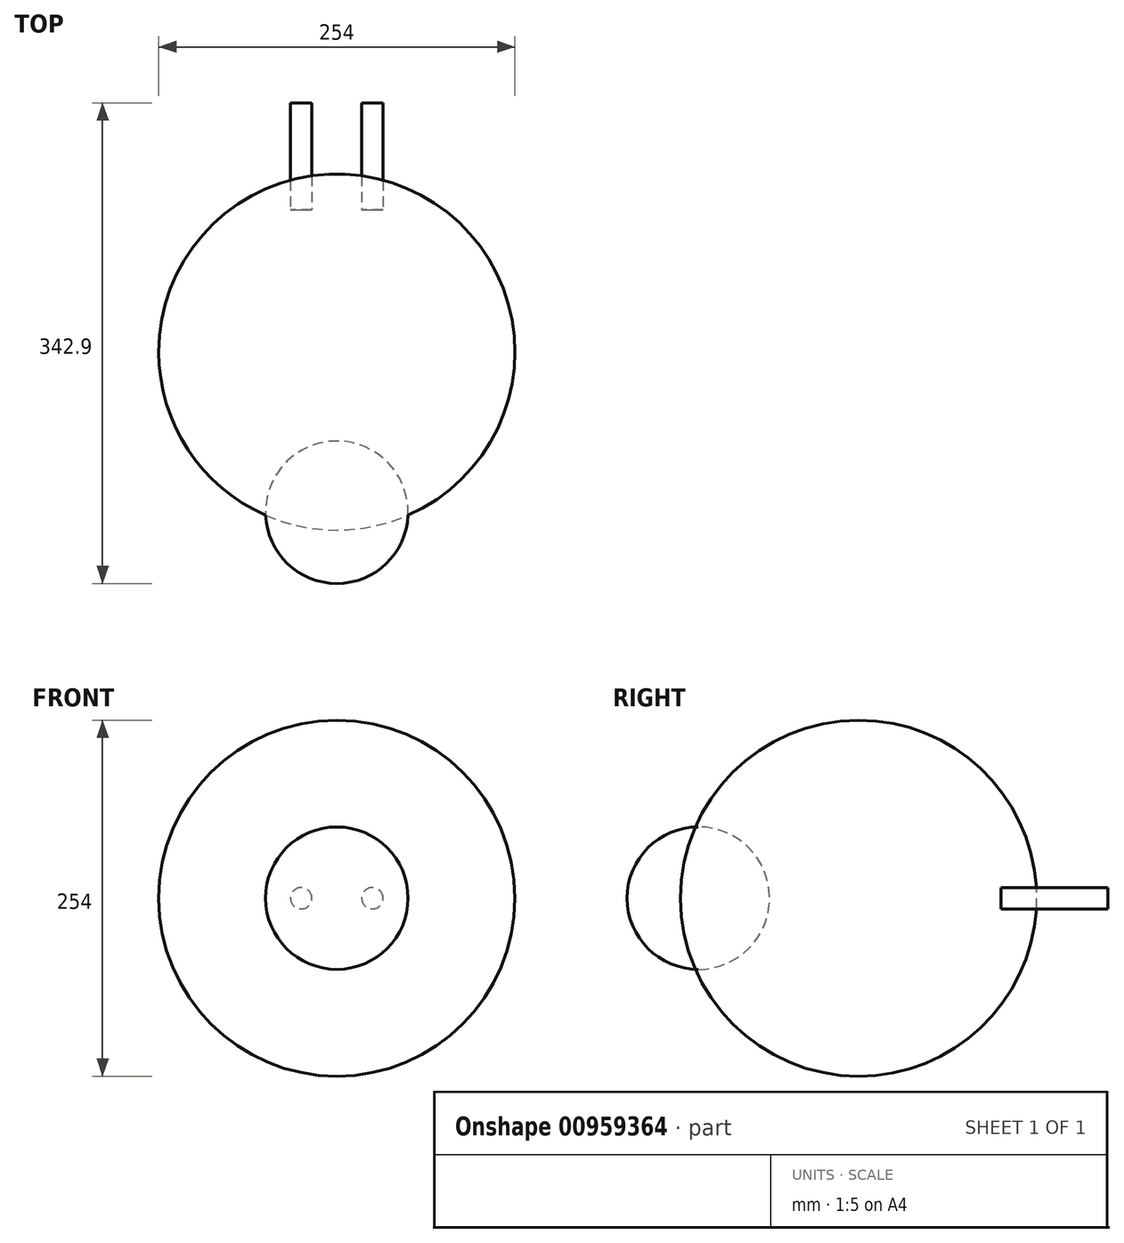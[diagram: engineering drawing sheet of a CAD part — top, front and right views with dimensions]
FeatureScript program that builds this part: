
annotation { "Feature Type Name" : "Feature", "Feature Type Description" : "" }
export const myFeature = defineFeature(function(context is Context, id is Id, definition is map)
    precondition{}
    {
        {
            var Q0;
            Q0=qCreatedBy(makeId("Front.planeOp"),FACE);
            var sketch = newSketch(context, id + "F0", { "sketchPlane" : qUnion([Q0])});
            skArc(sketch, "E0", {"start": v(0, -127) * mm, "mid": v(127, 0) * mm, "end": v(0, 127) * mm});
            skLineSegment(sketch, "E1", {"start": v(0, 127) * mm, "end": v(0, -127) * mm});
            skSolve(sketch);
        }
        {
            var Q0;
            Q0=makeQuery(id+"F0.imprint","IMPRINT",FACE,{"disambiguationData":[TD([[makeQuery(id+"F0.imprint","IMPRINT",EDGE,{"derivedFrom":sQuery(id+"F0.wireOp",EDGE,"E0")}),1.0]])]});
            var Q1;
            Q1=sQuery(id+"F0.wireOp",EDGE,"E1");
            revolve(context, id + "F1", {"surfaceOperationType" : NewSurfaceOperationType.NEW, "entities" : qUnion([Q0]), "axis" : qUnion([Q1]), "revolveType" : RevolveType.FULL});
        }
        {
            var Q0;
            Q0=makeQuery(id+"F0.imprint","IMPRINT",FACE,{"disambiguationData":[TD([[makeQuery(id+"F0.imprint","IMPRINT",EDGE,{"derivedFrom":sQuery(id+"F0.wireOp",EDGE,"E0")}),1.0]])]});
            cPlane(context, id + "F2", {"entities" : qUnion([Q0]), "cplaneType" : CPlaneType.OFFSET, "offset" : 114.3 * mm, "width" : 152.4 * mm, "height" : 152.4 * mm});
        }
        {
            var Q0;
            Q0=qCreatedBy(id+"F2.planeOp",FACE);
            var sketch = newSketch(context, id + "F3", { "sketchPlane" : qUnion([Q0])});
            skArc(sketch, "E2", {"start": v(0, -50.8) * mm, "mid": v(50.8, 0) * mm, "end": v(0, 50.8) * mm});
            skLineSegment(sketch, "E3", {"start": v(0, 50.8) * mm, "end": v(0, -50.8) * mm});
            skSolve(sketch);
        }
        {
            var Q0;
            Q0=makeQuery(id+"F3.imprint","IMPRINT",FACE,{"disambiguationData":[TD([[makeQuery(id+"F3.imprint","IMPRINT",EDGE,{"derivedFrom":sQuery(id+"F3.wireOp",EDGE,"E2")}),1.0]])]});
            var Q1;
            Q1=sQuery(id+"F3.wireOp",EDGE,"E3");
            revolve(context, id + "F4", {"surfaceOperationType" : NewSurfaceOperationType.NEW, "entities" : qUnion([Q0]), "axis" : qUnion([Q1]), "revolveType" : RevolveType.FULL});
        }
        {
            var Q0;
            Q0=qCreatedBy(makeId("Top.planeOp"),FACE);
            cPlane(context, id + "F5", {"entities" : qUnion([Q0]), "cplaneType" : CPlaneType.OFFSET, "offset" : 0 * mm, "oppositeDirection" : true, "width" : 152.4 * mm, "height" : 152.4 * mm});
        }
        {
            var Q0;
            Q0=qCreatedBy(id+"F5.planeOp",FACE);
            var sketch = newSketch(context, id + "F6", { "sketchPlane" : qUnion([Q0])});
            skLineSegment(sketch, "E4.bottom", {"start": v(-33.02, 101.6) * mm, "end": v(-25.4, 101.6) * mm});
            skLineSegment(sketch, "E4.top", {"start": v(-33.02, 177.8) * mm, "end": v(-25.4, 177.8) * mm});
            skLineSegment(sketch, "E4.left", {"start": v(-33.02, 101.6) * mm, "end": v(-33.02, 177.8) * mm});
            skLineSegment(sketch, "E4.right", {"start": v(-25.4, 101.6) * mm, "end": v(-25.4, 177.8) * mm});
            skLineSegment(sketch, "E5.bottom", {"start": v(25.4, 101.6) * mm, "end": v(33.02, 101.6) * mm});
            skLineSegment(sketch, "E5.top", {"start": v(25.4, 177.8) * mm, "end": v(33.02, 177.8) * mm});
            skLineSegment(sketch, "E5.left", {"start": v(25.4, 101.6) * mm, "end": v(25.4, 177.8) * mm});
            skLineSegment(sketch, "E5.right", {"start": v(33.02, 101.6) * mm, "end": v(33.02, 177.8) * mm});
            skSolve(sketch);
        }
        {
            var Q0;
            Q0=makeQuery(id+"F6.imprint","IMPRINT",FACE,{"disambiguationData":[TD([[makeQuery(id+"F6.imprint","IMPRINT",EDGE,{"derivedFrom":sQuery(id+"F6.wireOp",EDGE,"E4.bottom")}),1.0]])]});
            var Q1;
            Q1=sQuery(id+"F6.wireOp",EDGE,"E4.right");
            revolve(context, id + "F7", {"surfaceOperationType" : NewSurfaceOperationType.NEW, "entities" : qUnion([Q0]), "axis" : qUnion([Q1]), "revolveType" : RevolveType.FULL});
        }
        {
            var Q0;
            Q0=makeQuery(id+"F6.imprint","IMPRINT",FACE,{"disambiguationData":[TD([[makeQuery(id+"F6.imprint","IMPRINT",EDGE,{"derivedFrom":sQuery(id+"F6.wireOp",EDGE,"E5.bottom")}),1.0]])]});
            var Q1;
            Q1=sQuery(id+"F6.wireOp",EDGE,"E5.left");
            revolve(context, id + "F8", {"surfaceOperationType" : NewSurfaceOperationType.NEW, "entities" : qUnion([Q0]), "axis" : qUnion([Q1]), "revolveType" : RevolveType.FULL});
        }
    });
